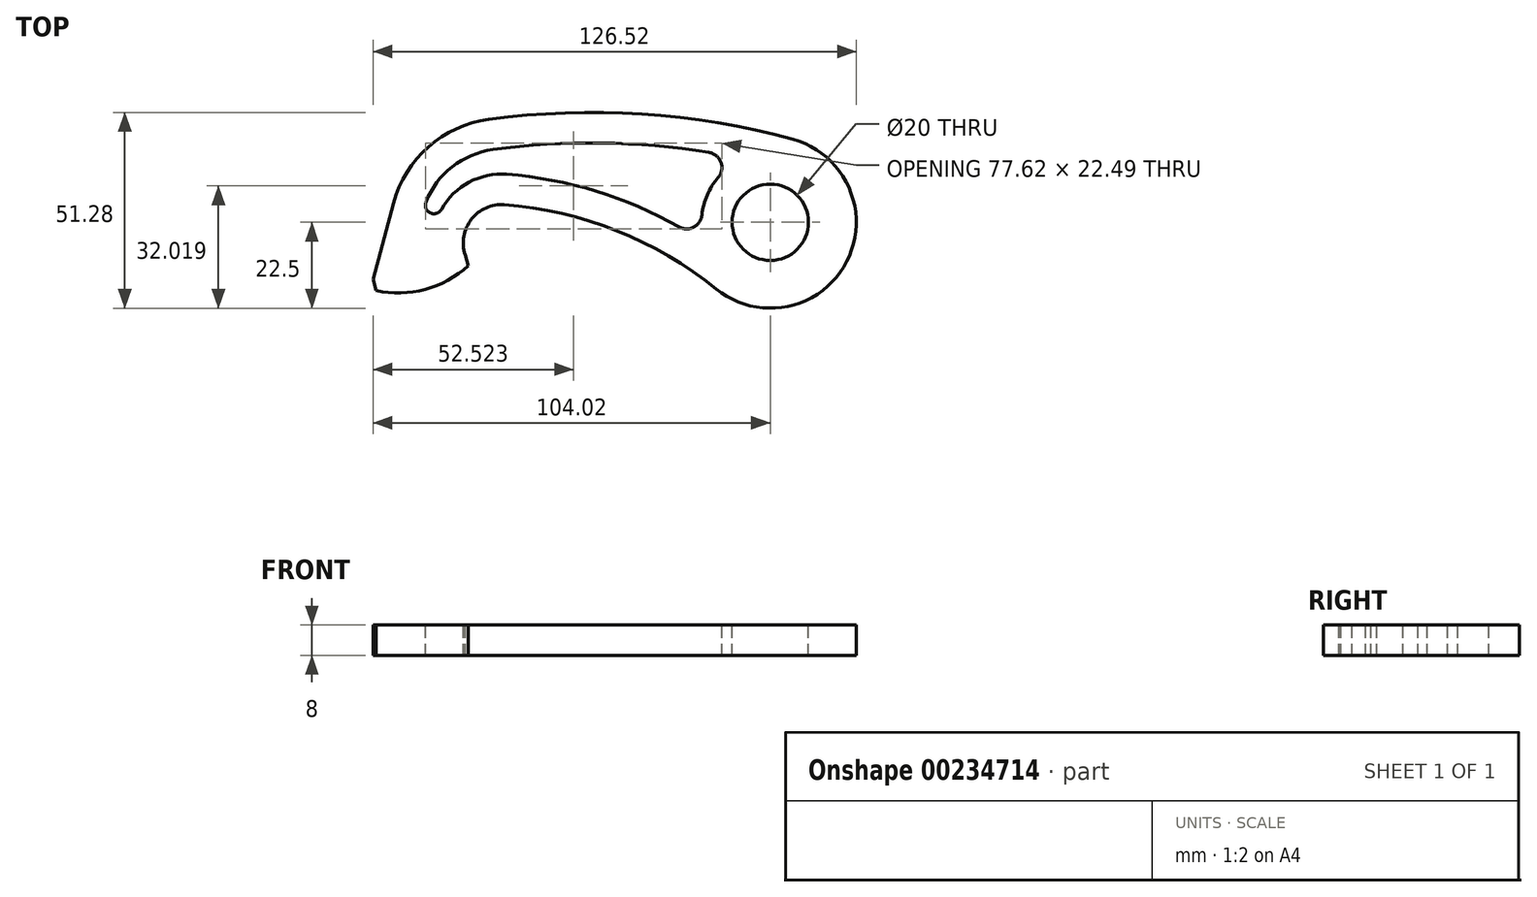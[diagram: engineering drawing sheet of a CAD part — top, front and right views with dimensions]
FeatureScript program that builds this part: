
annotation { "Feature Type Name" : "Feature", "Feature Type Description" : "" }
export const myFeature = defineFeature(function(context is Context, id is Id, definition is map)
    precondition{}
    {
        {
            var Q0;
            Q0=qCreatedBy(makeId("Top.planeOp"),FACE);
            var sketch = newSketch(context, id + "F0", { "sketchPlane" : qUnion([Q0])});
            skArc(sketch, "E0", {"start": v(-14.18, -17.47) * mm, "mid": v(20.02, -10.28) * mm, "end": v(5.93, 21.7) * mm});
            skCircle(sketch, "E1", {"center": v(0, 0) * mm, "radius": 10 * mm});
            skLineSegment(sketch, "E2", {"start": v(-100, 23.28) * mm, "end": v(-100, -30.54) * mm, "construction": true});
            skLineSegment(sketch, "E3", {"start": v(-100, 0) * mm, "end": v(-98.66, 5) * mm});
            skPoint(sketch, "E3.startSnap0", {"position": v(-100, -3.63) * mm});
            skLineSegment(sketch, "E4", {"start": v(-100, 0) * mm, "end": v(-104.02, -15) * mm});
            skLineSegment(sketch, "E5", {"start": v(-104.02, -15) * mm, "end": v(-79.87, -8.53) * mm, "construction": true});
            skLineSegment(sketch, "E6.0", {"start": v(-103.24, -17.9) * mm, "end": v(-79.1, -11.43) * mm, "construction": true});
            skLineSegment(sketch, "E7", {"start": v(-104.02, -15) * mm, "end": v(-103.24, -17.9) * mm});
            skLineSegment(sketch, "E8", {"start": v(-79.87, -8.53) * mm, "end": v(-79.1, -11.43) * mm});
            skLineSegment(sketch, "E9.0", {"start": v(-102.47, -20.8) * mm, "end": v(-78.32, -14.33) * mm, "construction": true});
            skArc(sketch, "E10", {"start": v(-103.24, -17.9) * mm, "mid": v(-90.4, -17.56) * mm, "end": v(-79.1, -11.43) * mm});
            skPoint(sketch, "E10.third.point", {"position": v(-90.4, -17.56) * mm});
            skLineSegment(sketch, "E11", {"start": v(-103.24, -17.9) * mm, "end": v(-102.47, -20.8) * mm, "construction": true});
            skLineSegment(sketch, "E12", {"start": v(-79.1, -11.43) * mm, "end": v(-78.32, -14.33) * mm, "construction": true});
            skLineSegment(sketch, "E13.0", {"start": v(-77.96, -33.66) * mm, "end": v(-67.32, 6.07) * mm, "construction": true});
            skLineSegment(sketch, "E14", {"start": v(-98.66, 5) * mm, "end": v(-69.68, -2.76) * mm, "construction": true});
            skArc(sketch, "E15", {"start": v(-73.72, 26.96) * mm, "mid": v(-89.5, 19.75) * mm, "end": v(-98.66, 5) * mm});
            skArc(sketch, "E16.trimOffspring", {"start": v(-73.72, 26.96) * mm, "mid": v(-33.63, 28.35) * mm, "end": v(5.93, 21.7) * mm});
            skCircle(sketch, "E17", {"center": v(-79.87, -8.53) * mm, "radius": 10 * mm, "construction": true});
            skArc(sketch, "E18", {"start": v(-79.87, -8.53) * mm, "mid": v(-77.66, 1.48) * mm, "end": v(-67.8, 4.28) * mm});
            skArc(sketch, "E19", {"start": v(-14.18, -17.47) * mm, "mid": v(-40.22, -2.2) * mm, "end": v(-69.62, 4.6) * mm});
            skArc(sketch, "E20", {"start": v(-13.64, 11.74) * mm, "mid": v(-16.53, 7.13) * mm, "end": v(-17.9, 1.86) * mm});
            skArc(sketch, "E21.0", {"start": v(-72.64, 19.04) * mm, "mid": v(-44.31, 20.77) * mm, "end": v(-16.03, 18.3) * mm});
            skArc(sketch, "E22.0", {"start": v(-23.86, -1.2) * mm, "mid": v(-45.68, 8.18) * mm, "end": v(-69.02, 12.57) * mm});
            skArc(sketch, "E23.0", {"start": v(-72.64, 19.04) * mm, "mid": v(-83.26, 14.55) * mm, "end": v(-90.15, 5.3) * mm});
            skArc(sketch, "E24.0", {"start": v(-86.1, 3.4) * mm, "mid": v(-77.4, 11.2) * mm, "end": v(-65.72, 12.01) * mm});
            skArc(sketch, "E25.filletArc", {"start": v(-13.64, 11.74) * mm, "mid": v(-12.92, 15.72) * mm, "end": v(-16.03, 18.3) * mm});
            skArc(sketch, "E26.filletArc", {"start": v(-23.86, -1.2) * mm, "mid": v(-20.05, -1.28) * mm, "end": v(-17.9, 1.86) * mm});
            skArc(sketch, "E27", {"start": v(-90.15, 5.3) * mm, "mid": v(-89.02, 2.46) * mm, "end": v(-86.1, 3.4) * mm});
            skSolve(sketch);
        }
        {
            var Q0;
            Q0 = qSketchRegion(id + "F0", true);
            extrude(context, id + "F1", {"entities" : qUnion([Q0]), "oppositeDirection" : true, "depth" : 8 * mm});
        }
    });
